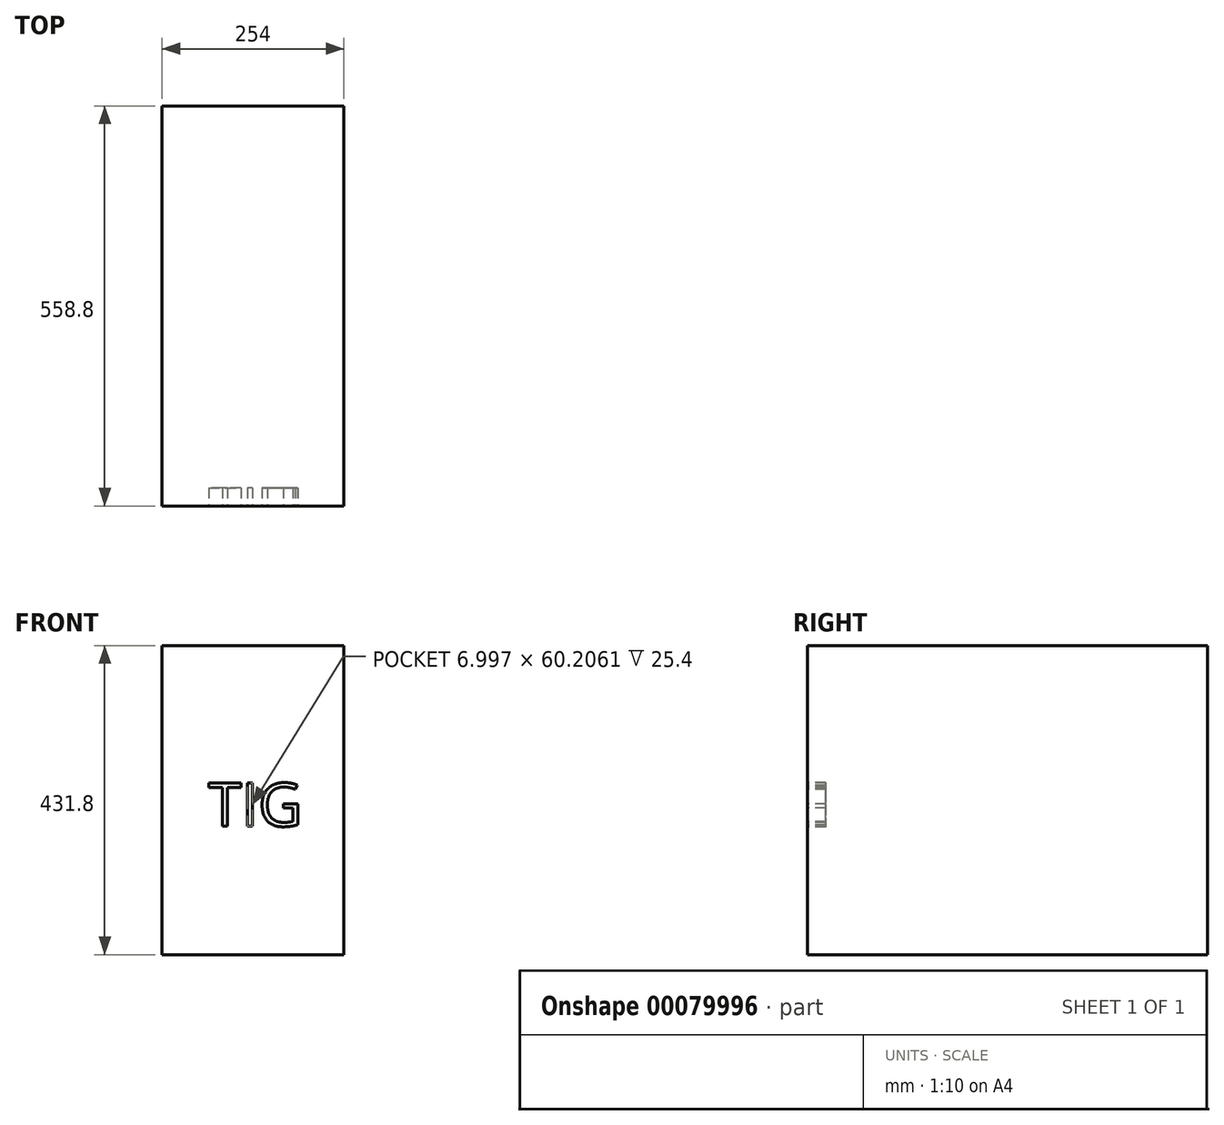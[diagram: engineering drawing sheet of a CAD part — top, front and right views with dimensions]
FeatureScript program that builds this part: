
annotation { "Feature Type Name" : "Feature", "Feature Type Description" : "" }
export const myFeature = defineFeature(function(context is Context, id is Id, definition is map)
    precondition{}
    {
        {
            var Q0;
            Q0=qCreatedBy(makeId("Front.planeOp"),FACE);
            var sketch = newSketch(context, id + "F0", { "sketchPlane" : qUnion([Q0])});
            skLineSegment(sketch, "E0.bottom", {"start": v(127, -215.9) * mm, "end": v(-127, -215.9) * mm});
            skLineSegment(sketch, "E0.top", {"start": v(127, 215.9) * mm, "end": v(-127, 215.9) * mm});
            skLineSegment(sketch, "E0.left", {"start": v(127, -215.9) * mm, "end": v(127, 215.9) * mm});
            skLineSegment(sketch, "E0.right", {"start": v(-127, -215.9) * mm, "end": v(-127, 215.9) * mm});
            skPoint(sketch, "E0.middle", {"position": v(0, 0) * mm});
            skSolve(sketch);
        }
        {
            var Q0;
            Q0=makeQuery(id+"F0.imprint","IMPRINT",FACE,{"disambiguationData":[TD([[makeQuery(id+"F0.imprint","IMPRINT",EDGE,{"derivedFrom":sQuery(id+"F0.wireOp",EDGE,"E0.bottom")}),-1.0]])]});
            extrude(context, id + "F1", {"entities" : qUnion([Q0]), "oppositeDirection" : true, "depth" : 558.8 * mm});
        }
        {
            var Q0;
            Q0=makeQuery(id+"F1.opExtrude","CAP_FACE",FACE,{"disambiguationData":[OSD([sQuery(id+"F0.wireOp",EDGE,"E0.bottom"),sQuery(id+"F0.wireOp",EDGE,"E0.top"),sQuery(id+"F0.wireOp",EDGE,"E0.left"),sQuery(id+"F0.wireOp",EDGE,"E0.right")])],"isStart":true});
            var sketch = newSketch(context, id + "F2", { "sketchPlane" : qUnion([Q0])});
            skText(sketch, "E1", { "text": "TIG", "fontName": "OpenSans-Regular.ttf"});
            const initialGuessF2  = {"E1": [-0.0627, -0.0366, 1, 0, 0.06072]};
            skSetInitialGuess(sketch, initialGuessF2);
            skSolve(sketch);
        }
        {
            var Q0;
            Q0 = qSketchRegion(id + "F2", true);
            extrude(context, id + "F3", {"entities" : qUnion([Q0]), "operationType" : NewBodyOperationType.REMOVE, "oppositeDirection" : true, "depth" : 25.4 * mm});
        }
    });
